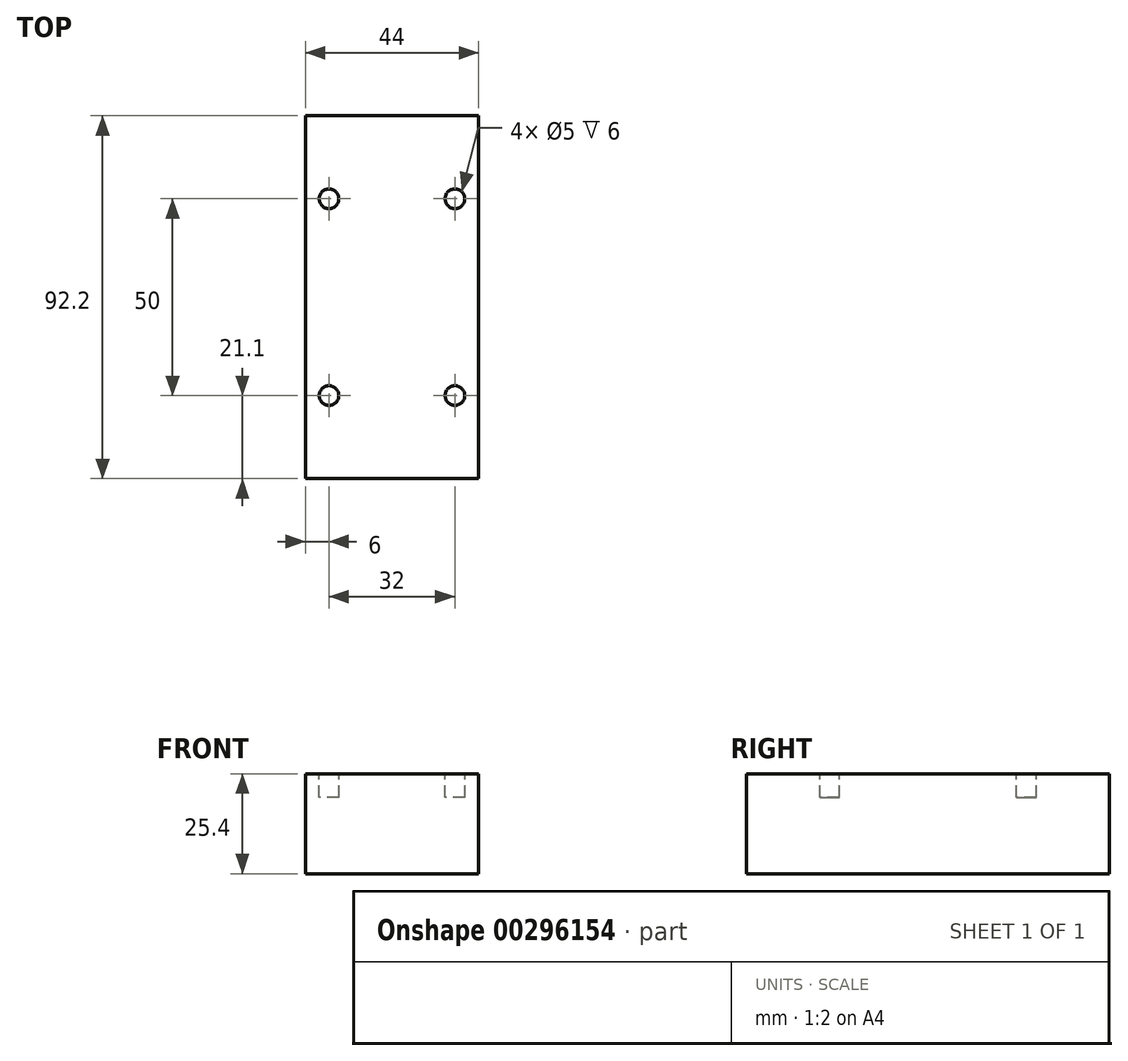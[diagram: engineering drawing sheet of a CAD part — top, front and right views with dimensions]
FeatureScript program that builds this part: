
annotation { "Feature Type Name" : "Feature", "Feature Type Description" : "" }
export const myFeature = defineFeature(function(context is Context, id is Id, definition is map)
    precondition{}
    {
        {
            var Q0;
            Q0=qCreatedBy(makeId("Front.planeOp"),FACE);
            var sketch = newSketch(context, id + "F0", { "sketchPlane" : qUnion([Q0])});
            skLineSegment(sketch, "E0.bottom", {"start": v(-22, 12.7) * mm, "end": v(22, 12.7) * mm});
            skLineSegment(sketch, "E0.top", {"start": v(-22, -12.7) * mm, "end": v(22, -12.7) * mm});
            skLineSegment(sketch, "E0.left", {"start": v(-22, 12.7) * mm, "end": v(-22, -12.7) * mm});
            skLineSegment(sketch, "E0.right", {"start": v(22, 12.7) * mm, "end": v(22, -12.7) * mm});
            skPoint(sketch, "E0.middle", {"position": v(0, 0) * mm});
            skSolve(sketch);
        }
        {
            var Q0;
            Q0=qSketchRegion(id+"F0",true);
            extrude(context, id + "F1", {"entities" : qUnion([Q0]), "oppositeDirection" : true, "depth" : 92.2 * mm});
        }
        {
            var Q0;
            Q0=makeQuery(id+"F1.opExtrude","SWEPT_FACE",FACE,{"disambiguationData":[OSD([sQuery(id+"F0.wireOp",EDGE,"E0.bottom")])]});
            var sketch = newSketch(context, id + "F2", { "sketchPlane" : qUnion([Q0])});
            skLineSegment(sketch, "E1.bottom", {"start": v(16, 118.22) * mm, "end": v(-16, 118.22) * mm, "construction": true});
            skLineSegment(sketch, "E1.top", {"start": v(16, -118.22) * mm, "end": v(-16, -118.22) * mm, "construction": true});
            skLineSegment(sketch, "E1.left", {"start": v(16, 118.22) * mm, "end": v(16, -118.22) * mm, "construction": true});
            skLineSegment(sketch, "E1.right", {"start": v(-16, 118.22) * mm, "end": v(-16, -118.22) * mm, "construction": true});
            skPoint(sketch, "E1.middle", {"position": v(0, 0) * mm});
            skLineSegment(sketch, "E2", {"start": v(-22, 46.1) * mm, "end": v(22, 46.1) * mm, "construction": true});
            skLineSegment(sketch, "E3.bottom", {"start": v(16, 71.1) * mm, "end": v(-41.41, 71.1) * mm, "construction": true});
            skLineSegment(sketch, "E3.top", {"start": v(16, 21.1) * mm, "end": v(-41.41, 21.1) * mm, "construction": true});
            skPoint(sketch, "E3.middle", {"position": v(-12.7, 46.1) * mm});
            skCircle(sketch, "E4", {"center": v(-16, 71.1) * mm, "radius": 2.5 * mm});
            skCircle(sketch, "E5", {"center": v(16, 71.1) * mm, "radius": 2.5 * mm});
            skCircle(sketch, "E6", {"center": v(-16, 21.1) * mm, "radius": 2.5 * mm});
            skCircle(sketch, "E7", {"center": v(16, 21.1) * mm, "radius": 2.5 * mm});
            skSolve(sketch);
        }
        {
            var Q0;
            Q0=makeQuery(id+"F2.imprint","IMPRINT",FACE,{"disambiguationData":[TD([[makeQuery(id+"F2.imprint","IMPRINT",EDGE,{"derivedFrom":sQuery(id+"F2.wireOp",EDGE,"E4")}),1.0]])]});
            var Q1;
            Q1=makeQuery(id+"F2.imprint","IMPRINT",FACE,{"disambiguationData":[TD([[makeQuery(id+"F2.imprint","IMPRINT",EDGE,{"derivedFrom":sQuery(id+"F2.wireOp",EDGE,"E6")}),1.0]])]});
            var Q2;
            Q2=makeQuery(id+"F2.imprint","IMPRINT",FACE,{"disambiguationData":[TD([[makeQuery(id+"F2.imprint","IMPRINT",EDGE,{"derivedFrom":sQuery(id+"F2.wireOp",EDGE,"E7")}),1.0]])]});
            var Q3;
            Q3=makeQuery(id+"F2.imprint","IMPRINT",FACE,{"disambiguationData":[TD([[makeQuery(id+"F2.imprint","IMPRINT",EDGE,{"derivedFrom":sQuery(id+"F2.wireOp",EDGE,"E5")}),1.0]])]});
            var Q4;
            Q4=sQuery(id+"F2.wireOp",EDGE,"E4");
            var Q5;
            Q5=sQuery(id+"F2.wireOp",EDGE,"E6");
            var Q6;
            Q6=sQuery(id+"F2.wireOp",EDGE,"E7");
            var Q7;
            Q7=sQuery(id+"F2.wireOp",EDGE,"E5");
            extrude(context, id + "F3", {"entities" : qUnion([Q0, Q1, Q2, Q3]), "operationType" : NewBodyOperationType.REMOVE, "surfaceEntities" : qUnion([Q4, Q5, Q6, Q7]), "oppositeDirection" : true, "depth" : 6 * mm});
        }
    });
